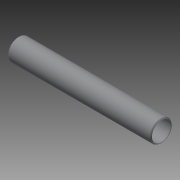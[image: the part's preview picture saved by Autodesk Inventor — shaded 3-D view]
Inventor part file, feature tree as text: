
AUTODESK INVENTOR PART (.ipt)
format: ipt  version: 2014 SP2 (Build 180246200, 246)  size: 135,680 bytes
history: native  units: in
note: dims shown in document units (in); Inventor stores cm internally (conversion verified against a paired STEP export)
features: other x42, revolve x1, sketch x1
ambient origin geometry x8: Origin, YZ Plane, XZ Plane, XY Plane, X Axis, Y Axis, Z Axis, Center Point
bodies: Solid1 (feature_tree)
feature tree (44):
  revolve  "Revolution1"  [1 undecoded]
  other  "cp1_XY"
  other  "cp1_YZ"
  other  "cp1_ZX"
  other  "cp1_X"
  other  "cp1_Y"
  other  "cp1_Z"
  other  "cp1_Center"
  other  "cp2_XY"
  other  "cp2_YZ"
  other  "cp2_ZX"
  other  "cp2_X"
  other  "cp2_Y"
  other  "cp2_Z"
  other  "cp2_Center"
  other  "cp3_XY"
  other  "cp3_YZ"
  other  "cp3_ZX"
  other  "cp3_X"
  other  "cp3_Y"
  other  "cp3_Z"
  other  "cp3_Center"
  other  "cp4_XY"
  other  "cp4_YZ"
  other  "cp4_ZX"
  other  "cp4_X"
  other  "cp4_Y"
  other  "cp4_Z"
  other  "cp4_Center"
  other  "tube_front_XY"
  other  "tube_front_YZ"
  other  "tube_front_ZX"
  other  "tube_front_X"
  other  "tube_front_Y"
  other  "tube_front_Z"
  other  "tube_front_Center"
  other  "tube_rear_XY"
  other  "tube_rear_YZ"
  other  "tube_rear_ZX"
  other  "tube_rear_X"
  other  "tube_rear_Y"
  other  "tube_rear_Z"
  other  "tube_rear_Center"
  sketch  "Sketch_1"  dims[d0=360.0deg]
note: 1 required parameter value undecoded (feature->parameter linkage not recoverable at this tier; creation-order binding heuristic only, values carry confidence <= 0.55)
